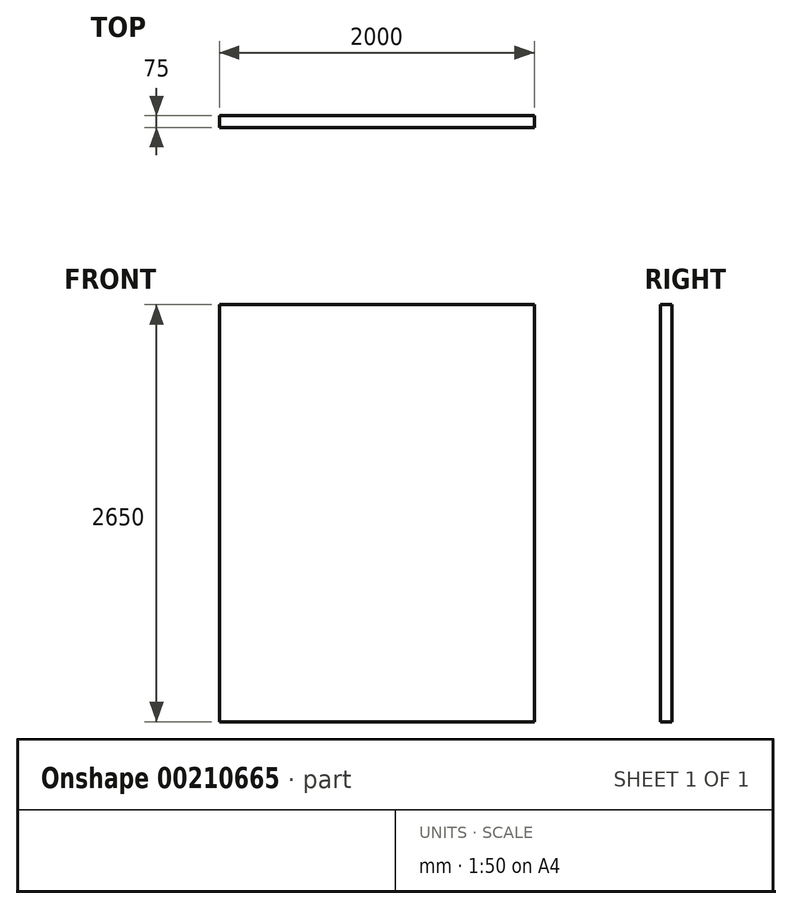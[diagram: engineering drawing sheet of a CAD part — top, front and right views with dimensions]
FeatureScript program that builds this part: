
annotation { "Feature Type Name" : "Feature", "Feature Type Description" : "" }
export const myFeature = defineFeature(function(context is Context, id is Id, definition is map)
    precondition{}
    {
        {
            var Q0;
            Q0=qCreatedBy(makeId("Front.planeOp"),FACE);
            var sketch = newSketch(context, id + "F0", { "sketchPlane" : qUnion([Q0])});
            skLineSegment(sketch, "E0.bottom", {"start": v(0, 0) * mm, "end": v(2000, 0) * mm});
            skLineSegment(sketch, "E0.top", {"start": v(0, 2650) * mm, "end": v(2000, 2650) * mm});
            skLineSegment(sketch, "E0.left", {"start": v(0, 0) * mm, "end": v(0, 2650) * mm});
            skLineSegment(sketch, "E0.right", {"start": v(2000, 0) * mm, "end": v(2000, 2650) * mm});
            skSolve(sketch);
        }
        {
            var Q0;
            Q0=makeQuery(id+"F0.imprint","IMPRINT",FACE,{"disambiguationData":[TD([[makeQuery(id+"F0.imprint","IMPRINT",EDGE,{"derivedFrom":sQuery(id+"F0.wireOp",EDGE,"E0.bottom")}),1.0]])]});
            extrude(context, id + "F1", {"entities" : qUnion([Q0]), "depth" : 75 * mm});
        }
    });
